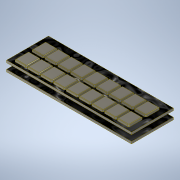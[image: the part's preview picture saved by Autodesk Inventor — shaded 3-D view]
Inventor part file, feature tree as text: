
AUTODESK INVENTOR PART (.ipt)
format: ipt  version: 2020 (Build 240168000, 168)  size: 647,680 bytes
history: native  units: mm
features: chamfer x16, extrude x10, sketch x10, other x2
ambient origin geometry x8: Origin, YZ Plane, XZ Plane, XY Plane, X Axis, Y Axis, Z Axis, Center Point
bodies: Body1 (feature_tree)
feature tree (38):
  other  "Bryła1"
  extrude  "Wyciągnięcie proste1"  Depth=10.5mm
  extrude  "Wyciągnięcie proste2"  Depth=55.88mm
  chamfer  "Faza1"  Distance=27.94mm
  chamfer  "Faza2"  Distance=1.0mm
  chamfer  "Faza3"  Distance=6.03mm
  extrude  "Wyciągnięcie proste3"  Depth=5.08mm
  chamfer  "Faza4"  Distance=2.54mm
  extrude  "Wyciągnięcie proste4"  Depth=1.27mm
  chamfer  "Faza5"  Distance=5.08mm
  chamfer  "Faza6"  Distance=6.03mm
  chamfer  "Faza7"  Distance=1.27mm
  chamfer  "Faza8"  Distance=0.64mm
  chamfer  "Faza9"  Distance=5.08mm
  chamfer  "Faza10"  Distance=0.64mm
  chamfer  "Faza11"  Distance=5.08mm
  chamfer  "Faza12"  Distance=0.64mm
  chamfer  "Faza13"  Distance=5.08mm
  chamfer  "Faza14"  Distance=0.64mm
  chamfer  "Faza15"  Distance=5.08mm
  chamfer  "Faza16"  Distance=5.08mm
  other  "Płaszczyzna konstrukcyjna1"
  extrude  "Wyciągnięcie proste5"  Depth=5.08mm
  extrude  "Wyciągnięcie proste6"  Depth=5.08mm
  extrude  "Wyciągnięcie proste7"  Depth=0.64mm
  extrude  "Wyciągnięcie proste8"  Depth=0.64mm
  extrude  "Wyciągnięcie proste9"  Depth=0.64mm
  extrude  "Extrusion10"  Depth=1.27mm
  sketch  "Szkic1"
  sketch  "Szkic2"
  sketch  "Szkic3"
  sketch  "Szkic4"
  sketch  "Szkic5"
  sketch  "Szkic6"
  sketch  "Szkic7"
  sketch  "Szkic8"
  sketch  "Szkic9"
  sketch  "Sketch10"  dims[d0=18.73mm d1=9.365mm d2=55.88mm d3=27.94mm d4=1.0mm d5=0.0mm d6=6.03mm d7=5.08mm d8=2.54mm d9=1.27mm d10=5.08mm d11=6.03mm d12=1.27mm d13=0.64mm d14=5.08mm d15=6.03mm d16=1.27mm d17=0.64mm d18=5.08mm d19=6.03mm d20=1.27mm d21=0.64mm d22=5.08mm d23=6.03mm d24=1.27mm d25=0.64mm d26=5.08mm d27=6.03mm d28=5.08mm d29=6.03mm d30=5.08mm d31=6.03mm d32=5.08mm d33=6.03mm d34=0.64mm d35=0.64mm d36=0.64mm d37=0.64mm d38=1.27mm d39=1.27mm d40=1.27mm d41=1.27mm d42=6.03mm d43=5.08mm d44=6.03mm d45=5.08mm d46=6.03mm d47=5.08mm d48=1.59mm d49=0.0mm d50=0.0mm d51=0.0mm d52=0.0mm d53=0.0mm d54=5.08mm d55=6.03mm d56=5.08mm d57=6.03mm d58=0.64mm d59=0.0mm d60=0.0mm d61=0.0mm d62=5.08mm d63=6.03mm d64=5.08mm d65=6.03mm d66=0.64mm d67=0.0mm d68=0.0mm d69=0.0mm d70=5.08mm d71=6.03mm d72=5.08mm d73=6.03mm d74=0.64mm d75=0.0mm d76=0.0mm d77=0.0mm d78=1.0mm d79=0.0mm d80=0.2mm d81=2.0mm d82=45.0deg d83=0.2mm d84=2.0mm d85=45.0deg d86=0.5mm d87=2.0mm d88=45.0deg d89=6.35mm d90=3.18mm d91=0.32mm d92=0.93mm d93=6.35mm d94=3.18mm d95=0.32mm d96=0.0mm d97=6.35mm d98=3.18mm d99=2.54mm d100=0.0mm d101=6.35mm d102=3.18mm d103=6.35mm d104=3.18mm d105=6.35mm d106=3.18mm d107=6.35mm d108=3.18mm d109=0.0mm d110=0.0mm d111=2.54mm d112=2.54mm d113=2.54mm d114=2.54mm d115=6.35mm d116=3.18mm d117=6.35mm d118=3.18mm d119=2.54mm d120=2.54mm d121=0.35mm d122=0.0mm d123=0.35mm d124=2.0mm d125=45.0deg d126=1.4mm d127=3.0mm d128=0.15mm d129=2.86mm d130=1.4mm d131=3.0mm d132=2.86mm d133=0.15mm d134=1.4mm d135=3.0mm d136=2.86mm d137=0.15mm d138=1.1mm d139=0.0mm d140=0.6mm d141=2.0mm d142=4.363323mm d143=0.6mm d144=2.0mm d145=4.363323mm d146=0.6mm d147=2.0mm d148=4.363323mm d149=0.6mm d150=2.0mm d151=4.363323mm d152=0.6mm d153=2.0mm d154=4.363323mm d155=0.6mm d156=2.0mm d157=4.363323mm d158=0.6mm d159=2.0mm d160=4.363323mm d161=0.6mm d162=2.0mm d163=4.363323mm d164=0.6mm d165=2.0mm d166=4.363323mm d167=0.6mm d168=2.0mm d169=4.363323mm d170=0.6mm d171=2.0mm d172=4.363323mm d173=0.6mm d174=2.0mm d175=4.363323mm d176=2.45mm d177=7.0mm d178=7.0mm d179=5.4mm d180=5.08mm d181=7.0mm d182=7.0mm d183=7.0mm d184=7.0mm d185=5.4mm d186=0.0mm d187=0.0mm d188=3.5mm d189=1.0mm d190=0.0mm d191=1.0mm d192=0.0mm d193=10.0mm d194=10.0mm d195=5.0mm d196=5.0mm d197=1.6mm d198=0.0mm d199=1.0mm d200=0.0mm d201=8.0mm d202=8.0mm d203=8.89mm d204=7.62mm d205=7.62mm d206=8.0mm d207=10.16mm d208=0.0mm d209=8.0mm d210=8.0mm d211=8.0mm d212=8.0mm d213=10.16mm d214=10.16mm d215=10.16mm d216=8.0mm d217=8.0mm d218=8.0mm d219=5.08mm d220=0.0mm d221=0.0mm d222=0.0mm d223=0.0mm d224=10.5mm d225=0.0mm d226=15.0mm d227=0.0mm]
